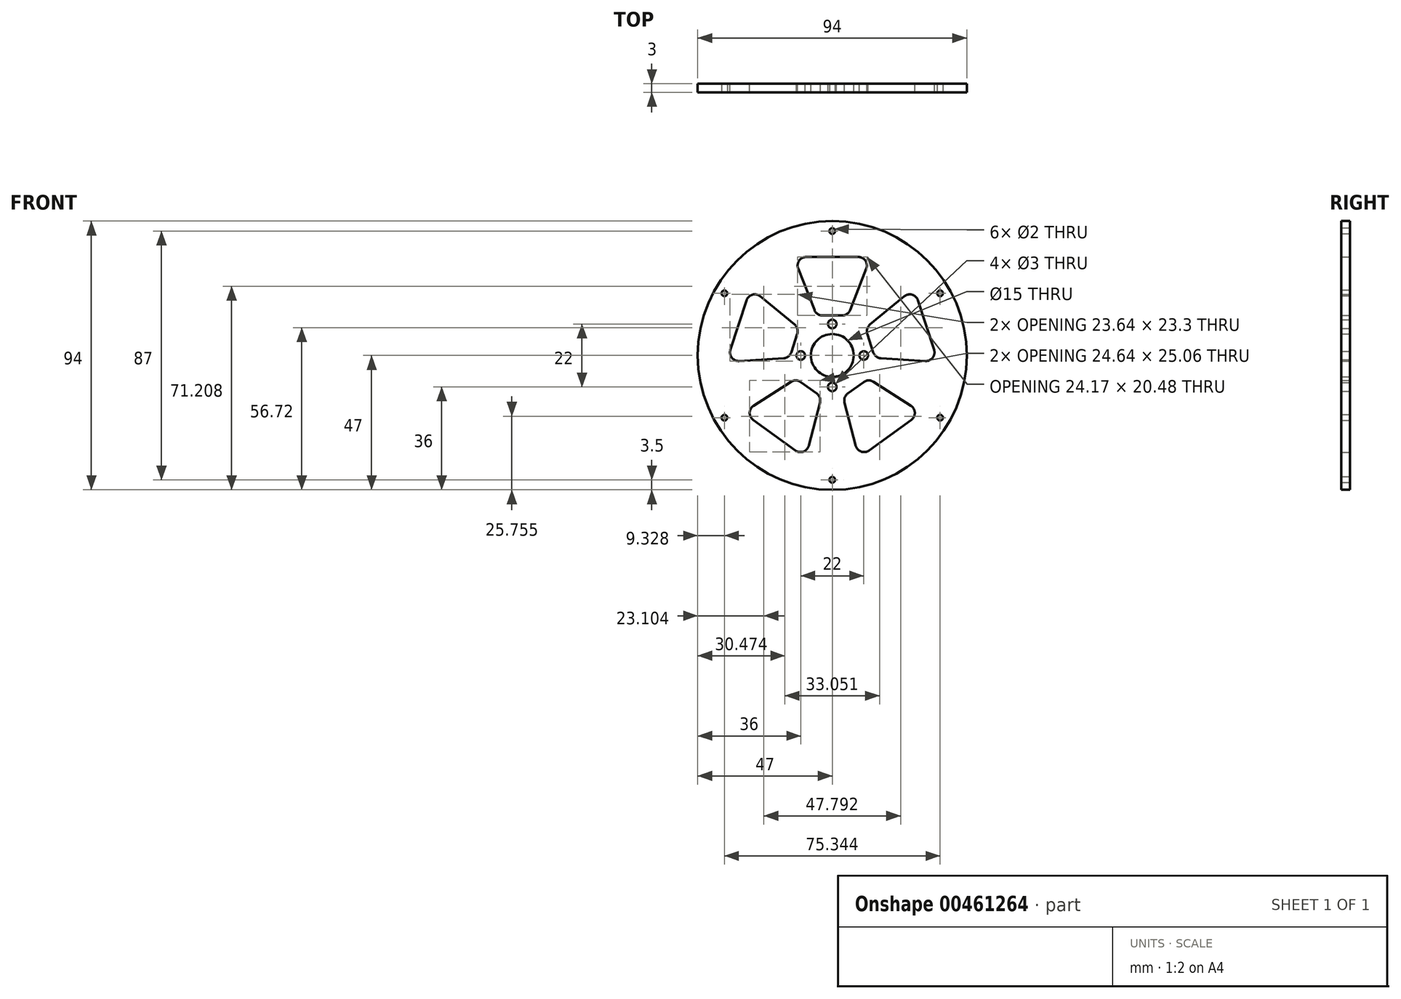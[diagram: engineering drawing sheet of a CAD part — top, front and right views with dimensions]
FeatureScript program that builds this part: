
annotation { "Feature Type Name" : "Feature", "Feature Type Description" : "" }
export const myFeature = defineFeature(function(context is Context, id is Id, definition is map)
    precondition{}
    {
        {
            var Q0;
            Q0=qCreatedBy(makeId("Front.planeOp"),FACE);
            var sketch = newSketch(context, id + "F0", { "sketchPlane" : qUnion([Q0])});
            skCircle(sketch, "E0", {"center": v(0, 0) * mm, "radius": 47 * mm});
            skCircle(sketch, "E1", {"center": v(0, 0) * mm, "radius": 7.5 * mm});
            skArc(sketch, "E2", {"start": v(5.47, 13.97) * mm, "mid": v(-8.82, -12.14) * mm, "end": v(11.6, 9.52) * mm});
            skCircle(sketch, "E3", {"center": v(0, 0) * mm, "radius": 37 * mm});
            skLineSegment(sketch, "E4", {"start": v(-11.9, 30.35) * mm, "end": v(-6.22, 15.87) * mm});
            skLineSegment(sketch, "E5.MirrorCS", {"start": v(11.9, 30.35) * mm, "end": v(6.22, 15.87) * mm});
            skLineSegment(sketch, "E6.1.0", {"start": v(-32.54, -1.93) * mm, "end": v(-17.02, -1.01) * mm});
            skLineSegment(sketch, "E6.1.1", {"start": v(-25.2, 20.7) * mm, "end": v(-13.17, 10.82) * mm});
            skArc(sketch, "E6.1.3", {"start": v(-5.47, 13.97) * mm, "mid": v(-3.78, -14.52) * mm, "end": v(11.6, 9.52) * mm});
            skLineSegment(sketch, "E6.2.0", {"start": v(-8.22, -31.55) * mm, "end": v(-4.3, -16.5) * mm});
            skLineSegment(sketch, "E6.2.1", {"start": v(-27.47, -17.57) * mm, "end": v(-14.36, -9.18) * mm});
            skArc(sketch, "E6.2.2", {"start": v(-28.6, 23.48) * mm, "mid": v(21.75, -29.93) * mm, "end": v(-13.5, 34.45) * mm});
            skCircle(sketch, "E6.2.3", {"center": v(0, 0) * mm, "radius": 15 * mm});
            skLineSegment(sketch, "E6.3.0", {"start": v(27.47, -17.57) * mm, "end": v(14.36, -9.18) * mm});
            skLineSegment(sketch, "E6.3.1", {"start": v(8.22, -31.55) * mm, "end": v(4.3, -16.5) * mm});
            skArc(sketch, "E6.3.2", {"start": v(-36.93, -2.2) * mm, "mid": v(21.75, -29.93) * mm, "end": v(13.5, 34.45) * mm});
            skArc(sketch, "E6.3.3", {"start": v(-14.97, -0.89) * mm, "mid": v(12.64, -8.08) * mm, "end": v(-5.47, 13.97) * mm});
            skLineSegment(sketch, "E6.4.0", {"start": v(25.2, 20.7) * mm, "end": v(13.17, 10.82) * mm});
            skLineSegment(sketch, "E6.4.1", {"start": v(32.54, -1.93) * mm, "end": v(17.02, -1.01) * mm});
            skArc(sketch, "E6.4.2", {"start": v(-28.6, 23.48) * mm, "mid": v(15.81, -33.45) * mm, "end": v(0, 37) * mm});
            skCircle(sketch, "E6.4.3", {"center": v(0, 0) * mm, "radius": 15 * mm});
            skPoint(sketch, "E7.start.orphan", {"position": v(0, 37) * mm});
            skArc(sketch, "E8.trimOffspring", {"start": v(0, 37) * mm, "mid": v(-6.87, 36.36) * mm, "end": v(-13.5, 34.45) * mm});
            skLineSegment(sketch, "E9", {"start": v(-9.1, 34.45) * mm, "end": v(9.1, 34.45) * mm});
            skLineSegment(sketch, "E10", {"start": v(-3.43, 13.97) * mm, "end": v(3.43, 13.97) * mm});
            skLineSegment(sketch, "E11", {"start": v(-29.95, 19.3) * mm, "end": v(-35.58, 1.99) * mm});
            skLineSegment(sketch, "E12", {"start": v(-12.22, 7.57) * mm, "end": v(-14.34, 1.06) * mm});
            skLineSegment(sketch, "E13", {"start": v(29.95, 19.3) * mm, "end": v(35.58, 1.99) * mm});
            skLineSegment(sketch, "E14", {"start": v(12.22, 7.57) * mm, "end": v(14.34, 1.06) * mm});
            skLineSegment(sketch, "E15", {"start": v(-27.61, -22.52) * mm, "end": v(-12.89, -33.22) * mm});
            skLineSegment(sketch, "E16", {"start": v(-5.44, -13.31) * mm, "end": v(-10.98, -9.28) * mm});
            skLineSegment(sketch, "E17", {"start": v(5.44, -13.31) * mm, "end": v(10.98, -9.28) * mm});
            skLineSegment(sketch, "E18", {"start": v(27.61, -22.52) * mm, "end": v(12.89, -33.22) * mm});
            skPoint(sketch, "E19.visualSharp", {"position": v(-13.5, 34.45) * mm});
            skArc(sketch, "E19.filletArc", {"start": v(-9.1, 34.45) * mm, "mid": v(-11.58, 33.14) * mm, "end": v(-11.9, 30.35) * mm});
            skPoint(sketch, "E20.visualSharp", {"position": v(13.5, 34.45) * mm});
            skArc(sketch, "E20.filletArc", {"start": v(11.9, 30.35) * mm, "mid": v(11.58, 33.14) * mm, "end": v(9.1, 34.45) * mm});
            skPoint(sketch, "E21.visualSharp", {"position": v(-5.47, 13.97) * mm});
            skArc(sketch, "E21.filletArc", {"start": v(-6.22, 15.87) * mm, "mid": v(-5.12, 14.49) * mm, "end": v(-3.43, 13.97) * mm});
            skPoint(sketch, "E22.visualSharp", {"position": v(5.47, 13.97) * mm});
            skArc(sketch, "E22.filletArc", {"start": v(3.43, 13.97) * mm, "mid": v(5.12, 14.49) * mm, "end": v(6.22, 15.87) * mm});
            skPoint(sketch, "E23.visualSharp", {"position": v(28.6, 23.48) * mm});
            skArc(sketch, "E23.filletArc", {"start": v(29.95, 19.3) * mm, "mid": v(27.94, 21.25) * mm, "end": v(25.2, 20.7) * mm});
            skPoint(sketch, "E24.visualSharp", {"position": v(36.93, -2.2) * mm});
            skArc(sketch, "E24.filletArc", {"start": v(32.54, -1.93) * mm, "mid": v(35.1, -0.77) * mm, "end": v(35.58, 1.99) * mm});
            skPoint(sketch, "E25.visualSharp", {"position": v(11.6, 9.52) * mm});
            skArc(sketch, "E25.filletArc", {"start": v(13.17, 10.82) * mm, "mid": v(12.2, 9.34) * mm, "end": v(12.22, 7.57) * mm});
            skPoint(sketch, "E26.visualSharp", {"position": v(14.97, -0.89) * mm});
            skArc(sketch, "E26.filletArc", {"start": v(14.34, 1.06) * mm, "mid": v(15.36, -0.39) * mm, "end": v(17.02, -1.01) * mm});
            skPoint(sketch, "E27.visualSharp", {"position": v(12.64, -8.08) * mm});
            skArc(sketch, "E27.filletArc", {"start": v(14.36, -9.18) * mm, "mid": v(12.66, -8.71) * mm, "end": v(10.98, -9.28) * mm});
            skPoint(sketch, "E28.visualSharp", {"position": v(31.17, -19.94) * mm});
            skArc(sketch, "E28.filletArc", {"start": v(27.61, -22.52) * mm, "mid": v(28.85, -20) * mm, "end": v(27.47, -17.57) * mm});
            skPoint(sketch, "E29.visualSharp", {"position": v(9.33, -35.8) * mm});
            skArc(sketch, "E29.filletArc", {"start": v(8.22, -31.55) * mm, "mid": v(10.11, -33.62) * mm, "end": v(12.89, -33.22) * mm});
            skPoint(sketch, "E30.visualSharp", {"position": v(3.78, -14.52) * mm});
            skArc(sketch, "E30.filletArc", {"start": v(5.44, -13.31) * mm, "mid": v(4.38, -14.73) * mm, "end": v(4.3, -16.5) * mm});
            skPoint(sketch, "E31.visualSharp", {"position": v(-3.78, -14.52) * mm});
            skArc(sketch, "E31.filletArc", {"start": v(-4.3, -16.5) * mm, "mid": v(-4.38, -14.73) * mm, "end": v(-5.44, -13.31) * mm});
            skPoint(sketch, "E32.visualSharp", {"position": v(-9.33, -35.8) * mm});
            skArc(sketch, "E32.filletArc", {"start": v(-12.89, -33.22) * mm, "mid": v(-10.11, -33.62) * mm, "end": v(-8.22, -31.55) * mm});
            skPoint(sketch, "E33.visualSharp", {"position": v(-31.17, -19.94) * mm});
            skArc(sketch, "E33.filletArc", {"start": v(-27.47, -17.57) * mm, "mid": v(-28.85, -20) * mm, "end": v(-27.61, -22.52) * mm});
            skPoint(sketch, "E34.visualSharp", {"position": v(-12.64, -8.08) * mm});
            skArc(sketch, "E34.filletArc", {"start": v(-10.98, -9.28) * mm, "mid": v(-12.66, -8.71) * mm, "end": v(-14.36, -9.18) * mm});
            skPoint(sketch, "E35.visualSharp", {"position": v(-36.93, -2.2) * mm});
            skArc(sketch, "E35.filletArc", {"start": v(-35.58, 1.99) * mm, "mid": v(-35.1, -0.77) * mm, "end": v(-32.54, -1.93) * mm});
            skPoint(sketch, "E36.visualSharp", {"position": v(-28.6, 23.48) * mm});
            skArc(sketch, "E36.filletArc", {"start": v(-25.2, 20.7) * mm, "mid": v(-27.94, 21.25) * mm, "end": v(-29.95, 19.3) * mm});
            skPoint(sketch, "E37.visualSharp", {"position": v(-11.6, 9.52) * mm});
            skArc(sketch, "E37.filletArc", {"start": v(-12.22, 7.57) * mm, "mid": v(-12.2, 9.34) * mm, "end": v(-13.17, 10.82) * mm});
            skPoint(sketch, "E38.visualSharp", {"position": v(-14.97, -0.89) * mm});
            skArc(sketch, "E38.filletArc", {"start": v(-17.02, -1.01) * mm, "mid": v(-15.36, -0.39) * mm, "end": v(-14.34, 1.06) * mm});
            skSolve(sketch);
        }
        {
            var Q0;
            Q0=makeQuery(id+"F0.imprint","IMPRINT",FACE,{"disambiguationData":[TD([[makeQuery(id+"F0.imprint","IMPRINT",EDGE,{"derivedFrom":sQuery(id+"F0.wireOp",EDGE,"E0")}),1.0]])]});
            var Q1;
            {var subQ8=sQuery(id+"F0.wireOp",EDGE,"E4");Q1=makeQuery(id+"F0.imprint","IMPRINT",FACE,{"disambiguationData":[TD([[makeQuery(id+"F0.imprint","IMPRINT",EDGE,{"derivedFrom":subQ8}),-1.0]])]});}
            var Q2;
            Q2=makeQuery(id+"F0.imprint","IMPRINT",FACE,{"disambiguationData":[TD([[makeQuery(id+"F0.imprint","IMPRINT",EDGE,{"derivedFrom":sQuery(id+"F0.wireOp",EDGE,"E1")}),-1.0]])]});
            extrude(context, id + "F1", {"entities" : qUnion([Q0, Q1, Q2]), "depth" : 3 * mm});
        }
        {
            var Q0;
            Q0=makeQuery(id+"F1.opExtrude","CAP_FACE",FACE,{"disambiguationData":[OSD([sQuery(id+"F0.wireOp",EDGE,"E0"),sQuery(id+"F0.wireOp",EDGE,"E1"),sQuery(id+"F0.wireOp",EDGE,"E4"),sQuery(id+"F0.wireOp",EDGE,"E5.MirrorCS"),sQuery(id+"F0.wireOp",EDGE,"E6.1.0"),sQuery(id+"F0.wireOp",EDGE,"E6.1.1"),sQuery(id+"F0.wireOp",EDGE,"E6.2.0"),sQuery(id+"F0.wireOp",EDGE,"E6.2.1"),sQuery(id+"F0.wireOp",EDGE,"E6.3.0"),sQuery(id+"F0.wireOp",EDGE,"E6.3.1"),sQuery(id+"F0.wireOp",EDGE,"E6.4.0"),sQuery(id+"F0.wireOp",EDGE,"E6.4.1"),sQuery(id+"F0.wireOp",EDGE,"E9"),sQuery(id+"F0.wireOp",EDGE,"E10"),sQuery(id+"F0.wireOp",EDGE,"E11"),sQuery(id+"F0.wireOp",EDGE,"E12"),sQuery(id+"F0.wireOp",EDGE,"E13"),sQuery(id+"F0.wireOp",EDGE,"E14"),sQuery(id+"F0.wireOp",EDGE,"E15"),sQuery(id+"F0.wireOp",EDGE,"E16"),sQuery(id+"F0.wireOp",EDGE,"E17"),sQuery(id+"F0.wireOp",EDGE,"E18"),sQuery(id+"F0.wireOp",EDGE,"E19.filletArc"),sQuery(id+"F0.wireOp",EDGE,"E20.filletArc"),sQuery(id+"F0.wireOp",EDGE,"E21.filletArc"),sQuery(id+"F0.wireOp",EDGE,"E22.filletArc"),sQuery(id+"F0.wireOp",EDGE,"E23.filletArc"),sQuery(id+"F0.wireOp",EDGE,"E24.filletArc"),sQuery(id+"F0.wireOp",EDGE,"E25.filletArc"),sQuery(id+"F0.wireOp",EDGE,"E26.filletArc"),sQuery(id+"F0.wireOp",EDGE,"E27.filletArc"),sQuery(id+"F0.wireOp",EDGE,"E28.filletArc"),sQuery(id+"F0.wireOp",EDGE,"E29.filletArc"),sQuery(id+"F0.wireOp",EDGE,"E30.filletArc"),sQuery(id+"F0.wireOp",EDGE,"E31.filletArc"),sQuery(id+"F0.wireOp",EDGE,"E32.filletArc"),sQuery(id+"F0.wireOp",EDGE,"E33.filletArc"),sQuery(id+"F0.wireOp",EDGE,"E34.filletArc"),sQuery(id+"F0.wireOp",EDGE,"E35.filletArc"),sQuery(id+"F0.wireOp",EDGE,"E36.filletArc"),sQuery(id+"F0.wireOp",EDGE,"E37.filletArc"),sQuery(id+"F0.wireOp",EDGE,"E38.filletArc")])],"isStart":false});
            var sketch = newSketch(context, id + "F2", { "sketchPlane" : qUnion([Q0])});
            skCircle(sketch, "E39.cCircle", {"center": v(0, 0) * mm, "radius": 43.5 * mm, "construction": true});
            skLineSegment(sketch, "E39.0", {"start": v(0, -43.5) * mm, "end": v(-37.67, -21.75) * mm});
            skLineSegment(sketch, "E39.1", {"start": v(-37.67, -21.75) * mm, "end": v(-37.67, 21.75) * mm});
            skLineSegment(sketch, "E39.2", {"start": v(-37.67, 21.75) * mm, "end": v(0, 43.5) * mm});
            skLineSegment(sketch, "E39.3", {"start": v(0, 43.5) * mm, "end": v(37.67, 21.75) * mm});
            skLineSegment(sketch, "E39.4", {"start": v(37.67, 21.75) * mm, "end": v(37.67, -21.75) * mm});
            skLineSegment(sketch, "E39.5", {"start": v(37.67, -21.75) * mm, "end": v(0, -43.5) * mm});
            skPoint(sketch, "E40", {"position": v(0, 43.5) * mm});
            skPoint(sketch, "E41", {"position": v(37.67, 21.75) * mm});
            skPoint(sketch, "E42", {"position": v(37.67, -21.75) * mm});
            skPoint(sketch, "E43", {"position": v(0, -43.5) * mm});
            skPoint(sketch, "E44", {"position": v(-37.67, -21.75) * mm});
            skPoint(sketch, "E45", {"position": v(-37.67, 21.75) * mm});
            skSolve(sketch);
        }
        {
            var Q0;
            Q0=sQuery(id+"F2.wireOp",VERTEX,"E39.4.start");
            var Q1;
            Q1=sQuery(id+"F2.wireOp",VERTEX,"E39.5.start");
            var Q2;
            Q2=sQuery(id+"F2.wireOp",VERTEX,"E39.0.start");
            var Q3;
            Q3=sQuery(id+"F2.wireOp",VERTEX,"E39.1.start");
            var Q4;
            Q4=sQuery(id+"F2.wireOp",VERTEX,"E45");
            var Q5;
            Q5=sQuery(id+"F2.wireOp",VERTEX,"E39.3.start");
            var Q6;
            Q6=makeQuery(id+"F1.opExtrude","SWEPT_BODY",BODY,{"disambiguationData":[OSD([sQuery(id+"F0.wireOp",EDGE,"E0"),sQuery(id+"F0.wireOp",EDGE,"E1"),sQuery(id+"F0.wireOp",EDGE,"E4"),sQuery(id+"F0.wireOp",EDGE,"E5.MirrorCS"),sQuery(id+"F0.wireOp",EDGE,"E6.1.0"),sQuery(id+"F0.wireOp",EDGE,"E6.1.1"),sQuery(id+"F0.wireOp",EDGE,"E6.2.0"),sQuery(id+"F0.wireOp",EDGE,"E6.2.1"),sQuery(id+"F0.wireOp",EDGE,"E6.3.0"),sQuery(id+"F0.wireOp",EDGE,"E6.3.1"),sQuery(id+"F0.wireOp",EDGE,"E6.4.0"),sQuery(id+"F0.wireOp",EDGE,"E6.4.1"),sQuery(id+"F0.wireOp",EDGE,"E9"),sQuery(id+"F0.wireOp",EDGE,"E10"),sQuery(id+"F0.wireOp",EDGE,"E11"),sQuery(id+"F0.wireOp",EDGE,"E12"),sQuery(id+"F0.wireOp",EDGE,"E13"),sQuery(id+"F0.wireOp",EDGE,"E14"),sQuery(id+"F0.wireOp",EDGE,"E15"),sQuery(id+"F0.wireOp",EDGE,"E16"),sQuery(id+"F0.wireOp",EDGE,"E17"),sQuery(id+"F0.wireOp",EDGE,"E18"),sQuery(id+"F0.wireOp",EDGE,"E19.filletArc"),sQuery(id+"F0.wireOp",EDGE,"E20.filletArc"),sQuery(id+"F0.wireOp",EDGE,"E21.filletArc"),sQuery(id+"F0.wireOp",EDGE,"E22.filletArc"),sQuery(id+"F0.wireOp",EDGE,"E23.filletArc"),sQuery(id+"F0.wireOp",EDGE,"E24.filletArc"),sQuery(id+"F0.wireOp",EDGE,"E25.filletArc"),sQuery(id+"F0.wireOp",EDGE,"E26.filletArc"),sQuery(id+"F0.wireOp",EDGE,"E27.filletArc"),sQuery(id+"F0.wireOp",EDGE,"E28.filletArc"),sQuery(id+"F0.wireOp",EDGE,"E29.filletArc"),sQuery(id+"F0.wireOp",EDGE,"E30.filletArc"),sQuery(id+"F0.wireOp",EDGE,"E31.filletArc"),sQuery(id+"F0.wireOp",EDGE,"E32.filletArc"),sQuery(id+"F0.wireOp",EDGE,"E33.filletArc"),sQuery(id+"F0.wireOp",EDGE,"E34.filletArc"),sQuery(id+"F0.wireOp",EDGE,"E35.filletArc"),sQuery(id+"F0.wireOp",EDGE,"E36.filletArc"),sQuery(id+"F0.wireOp",EDGE,"E37.filletArc"),sQuery(id+"F0.wireOp",EDGE,"E38.filletArc")])]});
            hole(context, id + "F3", {"style" : HoleStyle.SIMPLE, "endStyle" : HoleEndStyle.THROUGH, "holeDiameter" : 2 * mm, "isTappedThrough" : true, "tappedDepth" : 12 * mm, "tapClearance" : 3, "locations" : qUnion([Q0, Q1, Q2, Q3, Q4, Q5]), "scope" : qUnion([Q6])});
        }
        {
            var Q0;
            Q0=qCreatedBy(makeId("Front.planeOp"),FACE);
            var sketch = newSketch(context, id + "F4", { "sketchPlane" : qUnion([Q0])});
            skCircle(sketch, "E46", {"center": v(0, 0) * mm, "radius": 11 * mm});
            skPoint(sketch, "E47", {"position": v(0, 11) * mm});
            skPoint(sketch, "E48", {"position": v(11, 0) * mm});
            skPoint(sketch, "E49", {"position": v(0, -11) * mm});
            skPoint(sketch, "E50", {"position": v(-11, 0) * mm});
            skSolve(sketch);
        }
        {
            var Q0;
            Q0=sQuery(id+"F4.wireOp",VERTEX,"E47");
            var Q1;
            Q1=sQuery(id+"F4.wireOp",VERTEX,"E48");
            var Q2;
            Q2=sQuery(id+"F4.wireOp",VERTEX,"E49");
            var Q3;
            Q3=sQuery(id+"F4.wireOp",VERTEX,"E50");
            var Q4;
            Q4=makeQuery(id+"F1.opExtrude","SWEPT_BODY",BODY,{"disambiguationData":[OSD([sQuery(id+"F0.wireOp",EDGE,"E0"),sQuery(id+"F0.wireOp",EDGE,"E1"),sQuery(id+"F0.wireOp",EDGE,"E4"),sQuery(id+"F0.wireOp",EDGE,"E5.MirrorCS"),sQuery(id+"F0.wireOp",EDGE,"E6.1.0"),sQuery(id+"F0.wireOp",EDGE,"E6.1.1"),sQuery(id+"F0.wireOp",EDGE,"E6.2.0"),sQuery(id+"F0.wireOp",EDGE,"E6.2.1"),sQuery(id+"F0.wireOp",EDGE,"E6.3.0"),sQuery(id+"F0.wireOp",EDGE,"E6.3.1"),sQuery(id+"F0.wireOp",EDGE,"E6.4.0"),sQuery(id+"F0.wireOp",EDGE,"E6.4.1"),sQuery(id+"F0.wireOp",EDGE,"E9"),sQuery(id+"F0.wireOp",EDGE,"E10"),sQuery(id+"F0.wireOp",EDGE,"E11"),sQuery(id+"F0.wireOp",EDGE,"E12"),sQuery(id+"F0.wireOp",EDGE,"E13"),sQuery(id+"F0.wireOp",EDGE,"E14"),sQuery(id+"F0.wireOp",EDGE,"E15"),sQuery(id+"F0.wireOp",EDGE,"E16"),sQuery(id+"F0.wireOp",EDGE,"E17"),sQuery(id+"F0.wireOp",EDGE,"E18"),sQuery(id+"F0.wireOp",EDGE,"E19.filletArc"),sQuery(id+"F0.wireOp",EDGE,"E20.filletArc"),sQuery(id+"F0.wireOp",EDGE,"E21.filletArc"),sQuery(id+"F0.wireOp",EDGE,"E22.filletArc"),sQuery(id+"F0.wireOp",EDGE,"E23.filletArc"),sQuery(id+"F0.wireOp",EDGE,"E24.filletArc"),sQuery(id+"F0.wireOp",EDGE,"E25.filletArc"),sQuery(id+"F0.wireOp",EDGE,"E26.filletArc"),sQuery(id+"F0.wireOp",EDGE,"E27.filletArc"),sQuery(id+"F0.wireOp",EDGE,"E28.filletArc"),sQuery(id+"F0.wireOp",EDGE,"E29.filletArc"),sQuery(id+"F0.wireOp",EDGE,"E30.filletArc"),sQuery(id+"F0.wireOp",EDGE,"E31.filletArc"),sQuery(id+"F0.wireOp",EDGE,"E32.filletArc"),sQuery(id+"F0.wireOp",EDGE,"E33.filletArc"),sQuery(id+"F0.wireOp",EDGE,"E34.filletArc"),sQuery(id+"F0.wireOp",EDGE,"E35.filletArc"),sQuery(id+"F0.wireOp",EDGE,"E36.filletArc"),sQuery(id+"F0.wireOp",EDGE,"E37.filletArc"),sQuery(id+"F0.wireOp",EDGE,"E38.filletArc")])]});
            hole(context, id + "F5", {"style" : HoleStyle.SIMPLE, "endStyle" : HoleEndStyle.THROUGH, "oppositeDirection" : true, "holeDiameter" : 3 * mm, "isTappedThrough" : true, "tappedDepth" : 12 * mm, "tapClearance" : 3, "locations" : qUnion([Q0, Q1, Q2, Q3]), "scope" : qUnion([Q4])});
        }
    });
